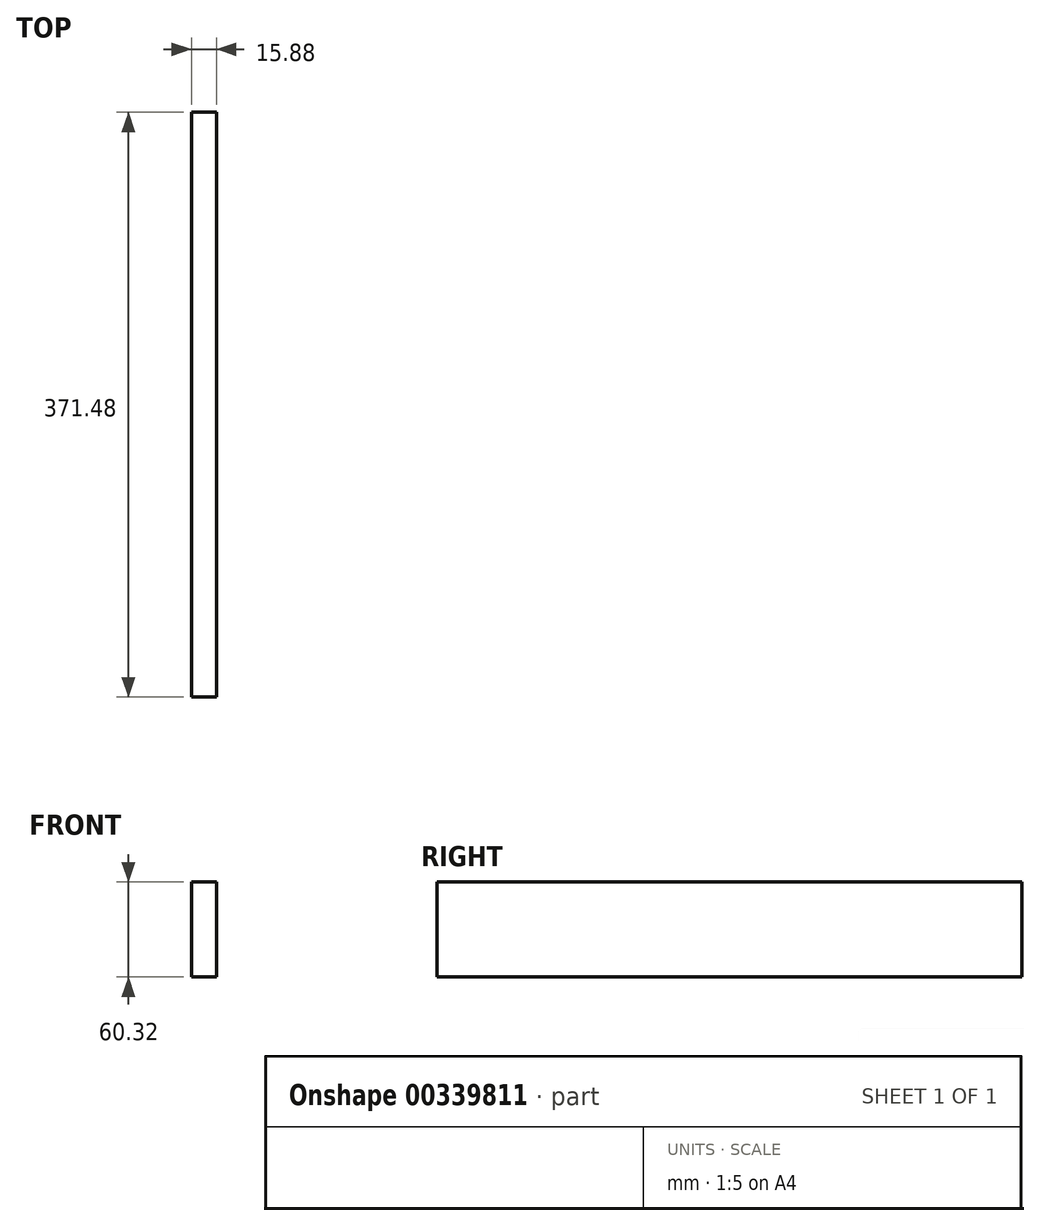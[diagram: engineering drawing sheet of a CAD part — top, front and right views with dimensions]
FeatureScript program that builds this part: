
annotation { "Feature Type Name" : "Feature", "Feature Type Description" : "" }
export const myFeature = defineFeature(function(context is Context, id is Id, definition is map)
    precondition{}
    {
        {
            var Q0;
            Q0=qCreatedBy(makeId("Right.planeOp"),FACE);
            var sketch = newSketch(context, id + "F0", { "sketchPlane" : qUnion([Q0])});
            skLineSegment(sketch, "E0.bottom", {"start": v(-96.33, 40.05) * mm, "end": v(275.15, 40.05) * mm});
            skLineSegment(sketch, "E0.top", {"start": v(-96.33, -20.27) * mm, "end": v(275.15, -20.27) * mm});
            skLineSegment(sketch, "E0.left", {"start": v(-96.33, 40.05) * mm, "end": v(-96.33, -20.27) * mm});
            skLineSegment(sketch, "E0.right", {"start": v(275.15, 40.05) * mm, "end": v(275.15, -20.27) * mm});
            skSolve(sketch);
        }
        {
            var Q0;
            Q0 = qSketchRegion(id + "F0", true);
            extrude(context, id + "F1", {"entities" : qUnion([Q0]), "oppositeDirection" : true, "depth" : 15.88 * mm});
        }
    });
